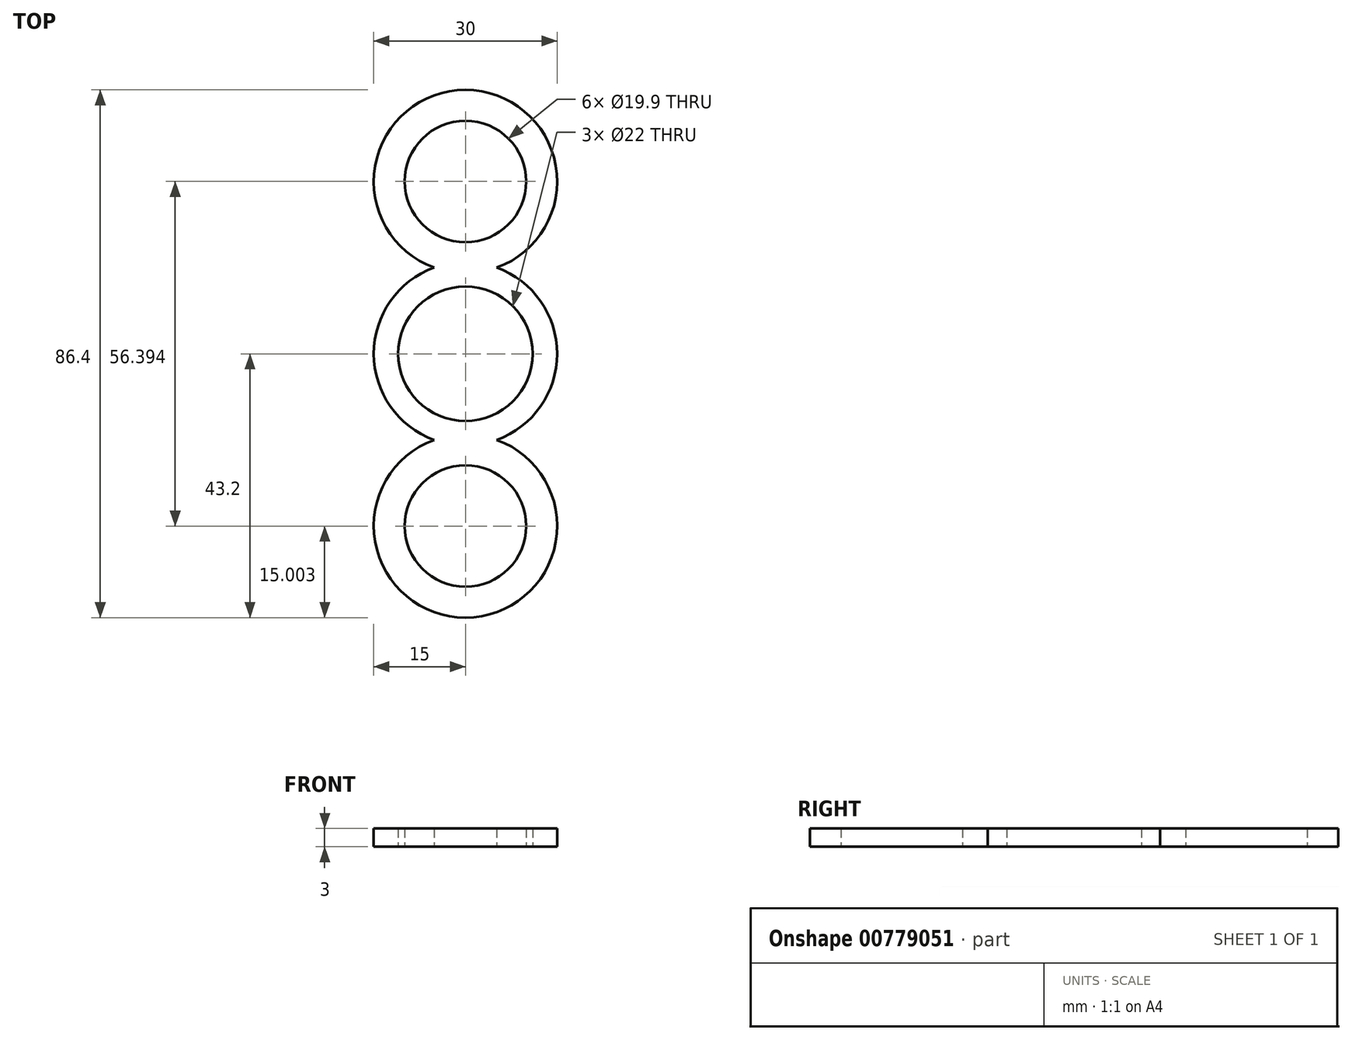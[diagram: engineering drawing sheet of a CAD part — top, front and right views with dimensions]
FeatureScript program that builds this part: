
annotation { "Feature Type Name" : "Feature", "Feature Type Description" : "" }
export const myFeature = defineFeature(function(context is Context, id is Id, definition is map)
    precondition{}
    {
        {
            var Q0;
            Q0=qCreatedBy(makeId("Top.planeOp"),FACE);
            var sketch = newSketch(context, id + "F0", { "sketchPlane" : qUnion([Q0])});
            skCircle(sketch, "E0", {"center": v(0, 0) * mm, "radius": 11 * mm});
            skArc(sketch, "E1", {"start": v(-5.12, 14.1) * mm, "mid": v(-15, 0) * mm, "end": v(-5.12, -14.1) * mm});
            skCircle(sketch, "E2", {"center": v(0, 28.2) * mm, "radius": 9.95 * mm});
            skArc(sketch, "E3", {"start": v(5.12, 14.1) * mm, "mid": v(0, 43.2) * mm, "end": v(-5.12, 14.1) * mm});
            skCircle(sketch, "E4", {"center": v(0, -28.2) * mm, "radius": 9.95 * mm});
            skArc(sketch, "E5", {"start": v(-5.12, -14.1) * mm, "mid": v(0, -43.2) * mm, "end": v(5.12, -14.1) * mm});
            skArc(sketch, "E6.trimOffspring", {"start": v(5.12, -14.1) * mm, "mid": v(15, 0) * mm, "end": v(5.12, 14.1) * mm});
            skSolve(sketch);
        }
        {
            var Q0;
            Q0 = qSketchRegion(id + "F0", true);
            extrude(context, id + "F1", {"entities" : qUnion([Q0]), "depth" : 3 * mm, "offsetDistance" : 25 * mm});
        }
    });
